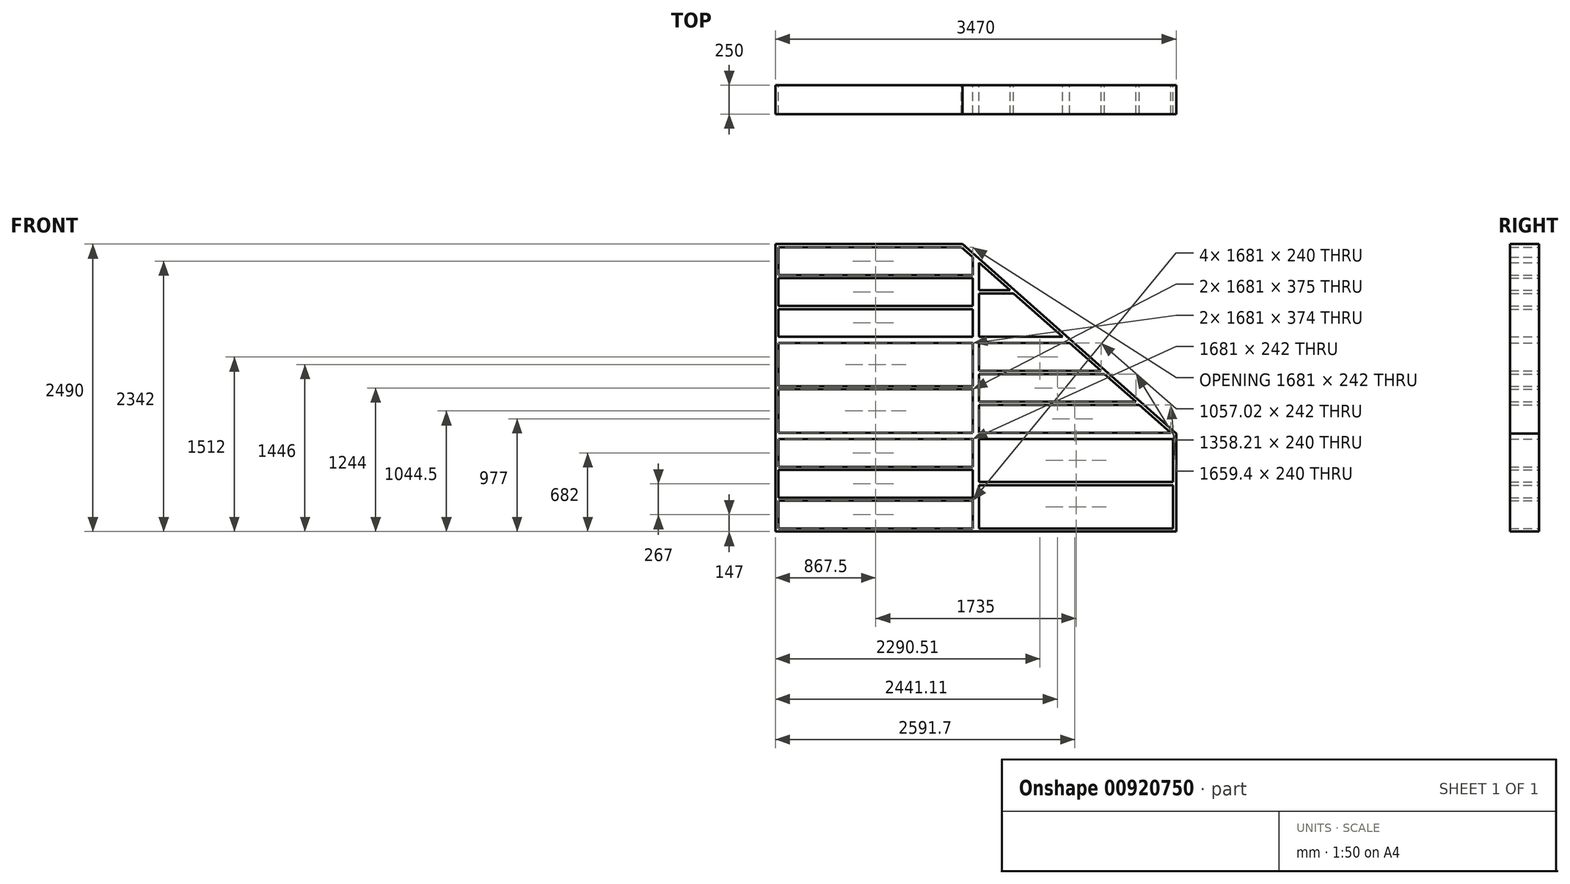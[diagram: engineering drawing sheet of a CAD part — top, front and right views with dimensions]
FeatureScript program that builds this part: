
annotation { "Feature Type Name" : "Feature", "Feature Type Description" : "" }
export const myFeature = defineFeature(function(context is Context, id is Id, definition is map)
    precondition{}
    {
        {
            var Q0;
            Q0=qCreatedBy(makeId("Front.planeOp"),FACE);
            var sketch = newSketch(context, id + "F0", { "sketchPlane" : qUnion([Q0])});
            skLineSegment(sketch, "E0.bottom", {"start": v(0, 0) * mm, "end": v(3470, 0) * mm});
            skLineSegment(sketch, "E0.top", {"start": v(0, 2490) * mm, "end": v(1620, 2490) * mm});
            skLineSegment(sketch, "E0.left", {"start": v(0, 0) * mm, "end": v(0, 2490) * mm});
            skLineSegment(sketch, "E0.right", {"start": v(3470, 0) * mm, "end": v(3470, 850) * mm});
            skLineSegment(sketch, "E1", {"start": v(1620, 2490) * mm, "end": v(3470, 850) * mm});
            skSolve(sketch);
        }
        {
            var Q0;
            Q0=makeQuery(id+"F0.imprint","IMPRINT",FACE,{"disambiguationData":[TD([[makeQuery(id+"F0.imprint","IMPRINT",EDGE,{"derivedFrom":sQuery(id+"F0.wireOp",EDGE,"E0.bottom")}),1.0]])]});
            var sketch = newSketch(context, id + "F1", { "sketchPlane" : qUnion([Q0])});
            skLineSegment(sketch, "E2.bottom", {"start": v(0, 0) * mm, "end": v(1735, 0) * mm});
            skLineSegment(sketch, "E2.top", {"start": v(0, 830) * mm, "end": v(1735, 830) * mm});
            skLineSegment(sketch, "E2.left", {"start": v(0, 0) * mm, "end": v(0, 830) * mm});
            skLineSegment(sketch, "E2.right", {"start": v(1735, 0) * mm, "end": v(1735, 830) * mm});
            skLineSegment(sketch, "E3.top", {"start": v(0, 1660) * mm, "end": v(1735, 1660) * mm});
            skLineSegment(sketch, "E3.left", {"start": v(0, 830) * mm, "end": v(0, 1660) * mm});
            skLineSegment(sketch, "E3.right", {"start": v(1735, 830) * mm, "end": v(1735, 1660) * mm});
            skLineSegment(sketch, "E4.0", {"start": v(27, 857) * mm, "end": v(27, 1232) * mm});
            skLineSegment(sketch, "E5.0", {"start": v(27, 1633) * mm, "end": v(1708, 1633) * mm});
            skLineSegment(sketch, "E6.0", {"start": v(1708, 857) * mm, "end": v(1708, 1232) * mm});
            skLineSegment(sketch, "E7.0", {"start": v(27, 857) * mm, "end": v(1708, 857) * mm});
            skLineSegment(sketch, "E8.bottom", {"start": v(27, 803) * mm, "end": v(1708, 803) * mm});
            skLineSegment(sketch, "E8.top", {"start": v(27, 27) * mm, "end": v(1708, 27) * mm});
            skLineSegment(sketch, "E8.left", {"start": v(27, 803) * mm, "end": v(27, 561) * mm});
            skLineSegment(sketch, "E8.right", {"start": v(1708, 803) * mm, "end": v(1708, 561) * mm});
            skLineSegment(sketch, "E9.0", {"start": v(1620, 2490) * mm, "end": v(3470, 850) * mm});
            skLineSegment(sketch, "E9.1", {"start": v(0, 2490) * mm, "end": v(1620, 2490) * mm});
            skLineSegment(sketch, "E9.2", {"start": v(3470, 0) * mm, "end": v(3470, 850) * mm});
            skLineSegment(sketch, "E10", {"start": v(0, 1660) * mm, "end": v(0, 2490) * mm});
            skLineSegment(sketch, "E11", {"start": v(1735, 1660) * mm, "end": v(1735, 2388.05) * mm});
            skLineSegment(sketch, "E12.bottom", {"start": v(1735, 830) * mm, "end": v(3470, 830) * mm});
            skLineSegment(sketch, "E12.top", {"start": v(1735, 0) * mm, "end": v(3470, 0) * mm});
            skLineSegment(sketch, "E12.left", {"start": v(1735, 830) * mm, "end": v(1735, 0) * mm});
            skLineSegment(sketch, "E12.right", {"start": v(3470, 830) * mm, "end": v(3470, 0) * mm});
            skLineSegment(sketch, "E13.top", {"start": v(1735, 1660) * mm, "end": v(2556.28, 1660) * mm});
            skLineSegment(sketch, "E13.right", {"start": v(3470, 830) * mm, "end": v(3470, 850) * mm});
            skLineSegment(sketch, "E14.bottom", {"start": v(1762, 803) * mm, "end": v(3443, 803) * mm});
            skLineSegment(sketch, "E14.top", {"start": v(1762, 27) * mm, "end": v(3443, 27) * mm});
            skLineSegment(sketch, "E14.left", {"start": v(1762, 803) * mm, "end": v(1762, 429) * mm});
            skLineSegment(sketch, "E14.right", {"start": v(3443, 803) * mm, "end": v(3443, 429) * mm});
            skLineSegment(sketch, "E15.bottom", {"start": v(1762, 1633) * mm, "end": v(2546.04, 1633) * mm});
            skLineSegment(sketch, "E15.top", {"start": v(1762, 857) * mm, "end": v(3421.4, 857) * mm});
            skLineSegment(sketch, "E15.left", {"start": v(1762, 1633) * mm, "end": v(1762, 1391) * mm});
            skLineSegment(sketch, "E16", {"start": v(2546.04, 1633) * mm, "end": v(2819.02, 1391) * mm});
            skLineSegment(sketch, "E17.bottom", {"start": v(27, 2463) * mm, "end": v(1609.76, 2463) * mm});
            skLineSegment(sketch, "E17.top", {"start": v(27, 1687) * mm, "end": v(1708, 1687) * mm});
            skLineSegment(sketch, "E17.left", {"start": v(27, 2463) * mm, "end": v(27, 2221) * mm});
            skLineSegment(sketch, "E18.bottom", {"start": v(1762, 1687) * mm, "end": v(2485.12, 1687) * mm});
            skLineSegment(sketch, "E18.left", {"start": v(1762, 1687) * mm, "end": v(1762, 2062) * mm});
            skLineSegment(sketch, "E19", {"start": v(1762, 2328.04) * mm, "end": v(2031.65, 2089) * mm});
            skLineSegment(sketch, "E20", {"start": v(1609.76, 2463) * mm, "end": v(1708, 2375.9) * mm});
            skLineSegment(sketch, "E21.trimOffspring", {"start": v(1708, 2375.9) * mm, "end": v(1708, 2221) * mm});
            skLineSegment(sketch, "E22.bottom", {"start": v(27, 561) * mm, "end": v(1708, 561) * mm});
            skLineSegment(sketch, "E22.top", {"start": v(27, 534) * mm, "end": v(1708, 534) * mm});
            skLineSegment(sketch, "E23.bottom", {"start": v(27, 1954) * mm, "end": v(1708, 1954) * mm});
            skLineSegment(sketch, "E23.top", {"start": v(27, 1927) * mm, "end": v(1708, 1927) * mm});
            skLineSegment(sketch, "E24.bottom", {"start": v(27, 2221) * mm, "end": v(1708, 2221) * mm});
            skLineSegment(sketch, "E24.top", {"start": v(27, 2194) * mm, "end": v(1708, 2194) * mm});
            skLineSegment(sketch, "E25.bottom", {"start": v(1762, 2089) * mm, "end": v(2031.65, 2089) * mm});
            skLineSegment(sketch, "E25.top", {"start": v(1762, 2062) * mm, "end": v(2062.1, 2062) * mm});
            skLineSegment(sketch, "E26.trimOffspring", {"start": v(1762, 2089) * mm, "end": v(1762, 2328.04) * mm});
            skLineSegment(sketch, "E27.trimOffspring", {"start": v(2062.1, 2062) * mm, "end": v(2485.12, 1687) * mm});
            skLineSegment(sketch, "E28.trimOffspring", {"start": v(27, 534) * mm, "end": v(27, 294) * mm});
            skLineSegment(sketch, "E29.trimOffspring", {"start": v(27, 2194) * mm, "end": v(27, 1954) * mm});
            skLineSegment(sketch, "E30.trimOffspring", {"start": v(27, 1927) * mm, "end": v(27, 1687) * mm});
            skLineSegment(sketch, "E31.trimOffspring", {"start": v(1708, 2194) * mm, "end": v(1708, 1954) * mm});
            skLineSegment(sketch, "E32.trimOffspring", {"start": v(1708, 1927) * mm, "end": v(1708, 1687) * mm});
            skLineSegment(sketch, "E33.bottom", {"start": v(1762, 429) * mm, "end": v(3443, 429) * mm});
            skLineSegment(sketch, "E33.top", {"start": v(1762, 402) * mm, "end": v(3443, 402) * mm});
            skLineSegment(sketch, "E34.bottom", {"start": v(27, 294) * mm, "end": v(1708, 294) * mm});
            skLineSegment(sketch, "E34.top", {"start": v(27, 267) * mm, "end": v(1708, 267) * mm});
            skLineSegment(sketch, "E35.bottom", {"start": v(27, 1259) * mm, "end": v(1708, 1259) * mm});
            skLineSegment(sketch, "E35.top", {"start": v(27, 1232) * mm, "end": v(1708, 1232) * mm});
            skLineSegment(sketch, "E36.bottom", {"start": v(1762, 1391) * mm, "end": v(2819.02, 1391) * mm});
            skLineSegment(sketch, "E36.top", {"start": v(1762, 1364) * mm, "end": v(2849.48, 1364) * mm});
            skLineSegment(sketch, "E37.bottom", {"start": v(1762, 1124) * mm, "end": v(3120.21, 1124) * mm});
            skLineSegment(sketch, "E37.top", {"start": v(1762, 1097) * mm, "end": v(3150.67, 1097) * mm});
            skLineSegment(sketch, "E38.trimOffspring", {"start": v(3150.67, 1097) * mm, "end": v(3421.4, 857) * mm});
            skLineSegment(sketch, "E39.trimOffspring", {"start": v(2849.48, 1364) * mm, "end": v(3120.21, 1124) * mm});
            skLineSegment(sketch, "E40.trimOffspring", {"start": v(1762, 1364) * mm, "end": v(1762, 1124) * mm});
            skLineSegment(sketch, "E41.trimOffspring", {"start": v(1762, 1097) * mm, "end": v(1762, 857) * mm});
            skLineSegment(sketch, "E42.trimOffspring", {"start": v(1708, 1259) * mm, "end": v(1708, 1633) * mm});
            skLineSegment(sketch, "E43.trimOffspring", {"start": v(27, 1259) * mm, "end": v(27, 1633) * mm});
            skLineSegment(sketch, "E44.trimOffspring", {"start": v(27, 267) * mm, "end": v(27, 27) * mm});
            skLineSegment(sketch, "E45.trimOffspring", {"start": v(1708, 267) * mm, "end": v(1708, 27) * mm});
            skLineSegment(sketch, "E46.trimOffspring", {"start": v(1708, 534) * mm, "end": v(1708, 294) * mm});
            skLineSegment(sketch, "E47.trimOffspring", {"start": v(1762, 402) * mm, "end": v(1762, 27) * mm});
            skLineSegment(sketch, "E48.trimOffspring", {"start": v(3443, 402) * mm, "end": v(3443, 27) * mm});
            skSolve(sketch);
        }
        {
            var Q0;
            Q0 = qSketchRegion(id + "F1", true);
            extrude(context, id + "F2", {"entities" : qUnion([Q0]), "depth" : 250 * mm, "offsetDistance" : 25 * mm});
        }
    });
